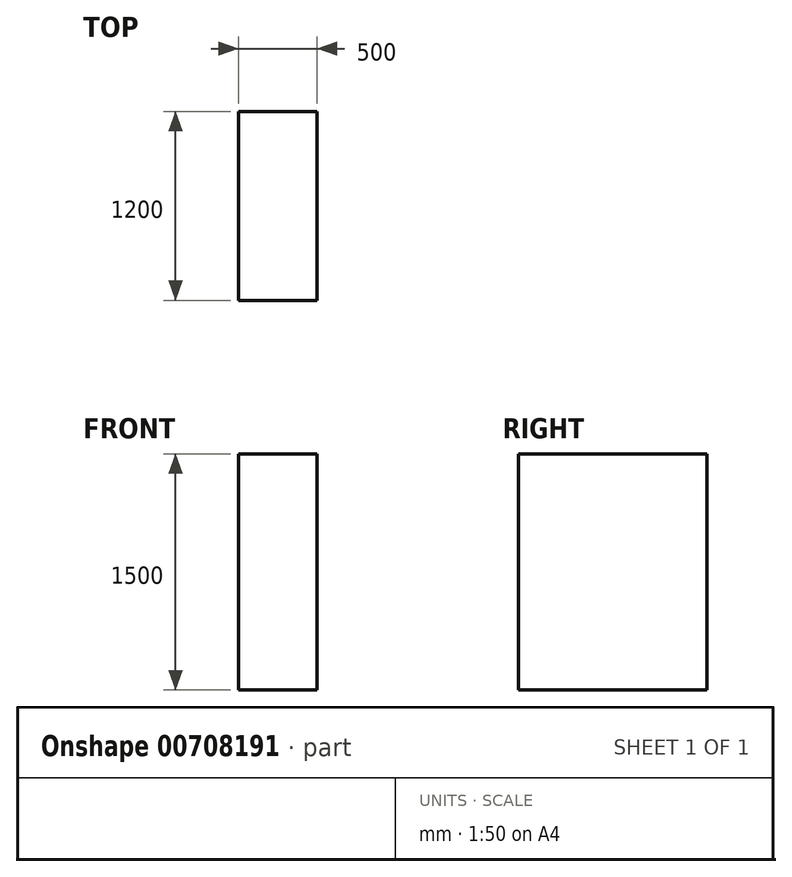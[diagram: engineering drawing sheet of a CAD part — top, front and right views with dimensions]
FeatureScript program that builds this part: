
annotation { "Feature Type Name" : "Feature", "Feature Type Description" : "" }
export const myFeature = defineFeature(function(context is Context, id is Id, definition is map)
    precondition{}
    {
        {
            var Q0;
            Q0=qCreatedBy(makeId("Top.planeOp"),FACE);
            var sketch = newSketch(context, id + "F0", { "sketchPlane" : qUnion([Q0])});
            skLineSegment(sketch, "E0.bottom", {"start": v(250, -600) * mm, "end": v(-250, -600) * mm});
            skLineSegment(sketch, "E0.top", {"start": v(250, 600) * mm, "end": v(-250, 600) * mm});
            skLineSegment(sketch, "E0.left", {"start": v(250, -600) * mm, "end": v(250, 600) * mm});
            skLineSegment(sketch, "E0.right", {"start": v(-250, -600) * mm, "end": v(-250, 600) * mm});
            skPoint(sketch, "E0.middle", {"position": v(0, 0) * mm});
            skSolve(sketch);
        }
        {
            var Q0;
            Q0=makeQuery(id+"F0.imprint","IMPRINT",FACE,{"disambiguationData":[TD([[makeQuery(id+"F0.imprint","IMPRINT",EDGE,{"derivedFrom":sQuery(id+"F0.wireOp",EDGE,"E0.bottom")}),-1.0]])]});
            extrude(context, id + "F1", {"entities" : qUnion([Q0]), "depth" : 1500 * mm, "offsetDistance" : 25 * mm});
        }
    });
